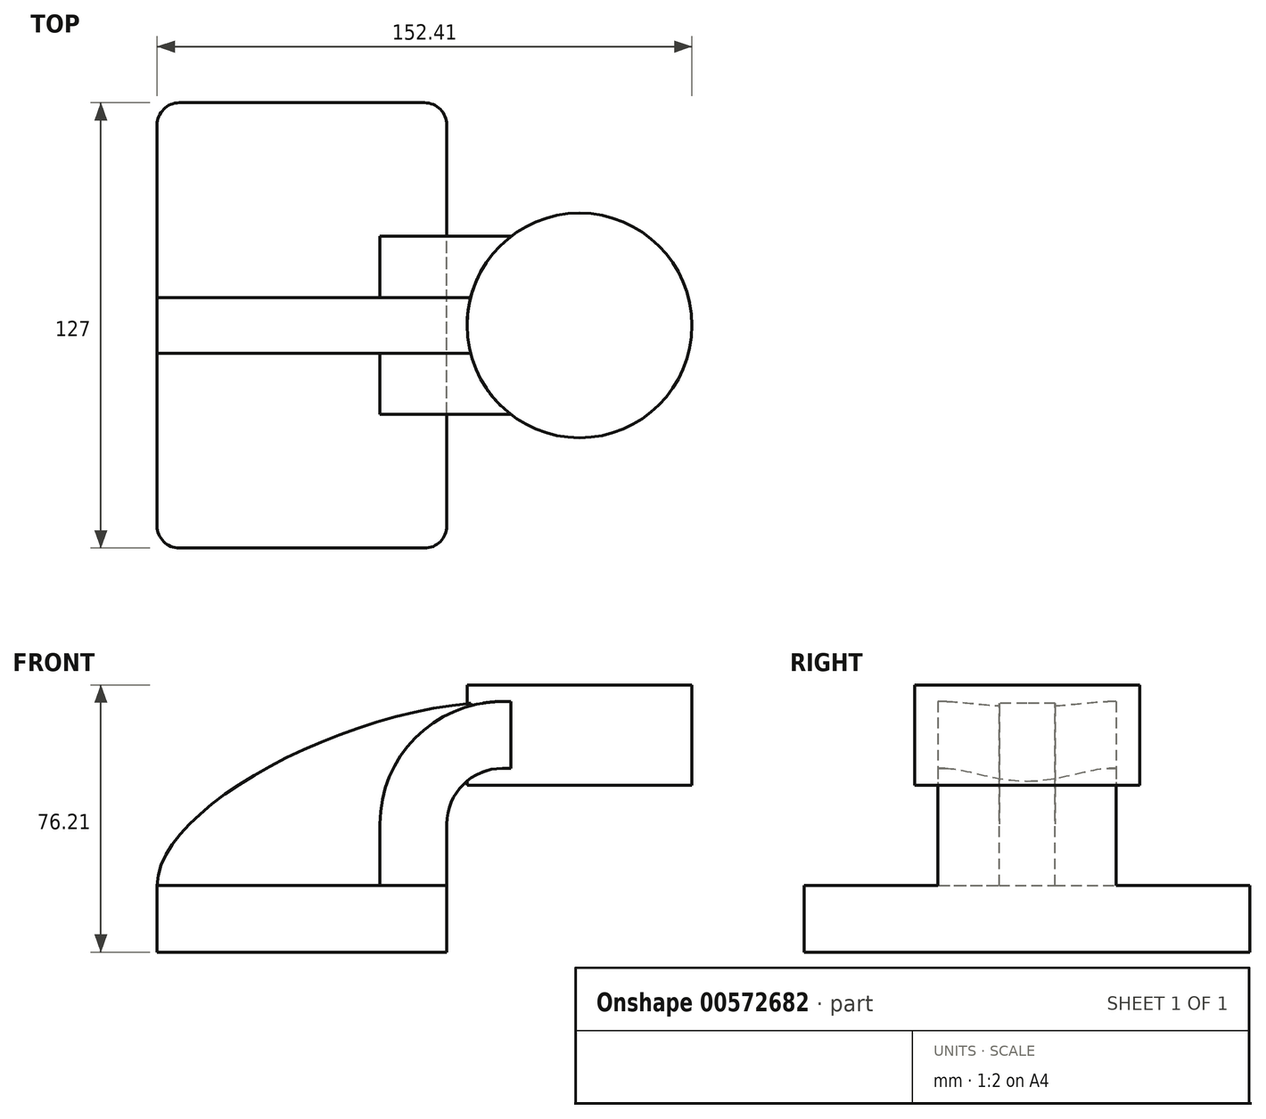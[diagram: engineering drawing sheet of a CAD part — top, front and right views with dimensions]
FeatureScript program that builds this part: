
annotation { "Feature Type Name" : "Feature", "Feature Type Description" : "" }
export const myFeature = defineFeature(function(context is Context, id is Id, definition is map)
    precondition{}
    {
        {
            var Q0;
            Q0=qCreatedBy(makeId("Front.planeOp"),FACE);
            var sketch = newSketch(context, id + "F0", { "sketchPlane" : qUnion([Q0])});
            skLineSegment(sketch, "E0.bottom", {"start": v(-41.28, -9.53) * mm, "end": v(41.28, -9.53) * mm});
            skLineSegment(sketch, "E0.top", {"start": v(-41.28, 9.53) * mm, "end": v(41.28, 9.53) * mm});
            skLineSegment(sketch, "E0.left", {"start": v(-41.28, -9.53) * mm, "end": v(-41.28, 9.53) * mm});
            skLineSegment(sketch, "E0.right", {"start": v(41.28, -9.53) * mm, "end": v(41.28, 9.53) * mm});
            skPoint(sketch, "E0.middle", {"position": v(0, 0) * mm});
            skLineSegment(sketch, "E1", {"start": v(41.28, 9.53) * mm, "end": v(41.28, 27) * mm});
            skArc(sketch, "E2", {"start": v(41.28, 27) * mm, "mid": v(45.92, 38.23) * mm, "end": v(57.15, 42.88) * mm});
            skLineSegment(sketch, "E3", {"start": v(57.15, 42.88) * mm, "end": v(78.82, 42.88) * mm});
            skLineSegment(sketch, "E4.bottom", {"start": v(60.32, 38.1) * mm, "end": v(111.12, 38.1) * mm});
            skLineSegment(sketch, "E4.top", {"start": v(60.32, 66.67) * mm, "end": v(111.12, 66.67) * mm});
            skLineSegment(sketch, "E4.left", {"start": v(60.32, 38.1) * mm, "end": v(60.32, 66.67) * mm});
            skLineSegment(sketch, "E4.right", {"start": v(111.12, 38.1) * mm, "end": v(111.12, 66.67) * mm});
            skPoint(sketch, "E4.middle", {"position": v(85.72, 52.39) * mm});
            skLineSegment(sketch, "E5.0", {"start": v(57.15, 61.93) * mm, "end": v(78.82, 61.93) * mm});
            skArc(sketch, "E5.1", {"start": v(22.23, 27) * mm, "mid": v(32.45, 51.7) * mm, "end": v(57.15, 61.93) * mm});
            skLineSegment(sketch, "E5.2", {"start": v(22.23, 9.53) * mm, "end": v(22.23, 27) * mm});
            skLineSegment(sketch, "E6", {"start": v(79.09, 38.1) * mm, "end": v(79.09, 66.67) * mm});
            skFitSpline(sketch, "E7", {"points": [v(-41.28, 9.53) * mm, v(57.15, 61.93) * mm], "startDerivative": vector(1.26, 69.94) * mm, "endDerivative": vector(123.61, 0.5) * mm});
            skSolve(sketch);
        }
        {
            var Q0;
            Q0=makeQuery(id+"F0.imprint","IMPRINT",FACE,{"disambiguationData":[TD([[makeQuery(id+"F0.imprint","IMPRINT",EDGE,{"derivedFrom":sQuery(id+"F0.wireOp",EDGE,"E0.bottom")}),1.0]])]});
            extrude(context, id + "F1", {"entities" : qUnion([Q0]), "endBound" : BoundingType.SYMMETRIC, "depth" : 127 * mm, "offsetDistance" : 25.4 * mm});
        }
        {
            var Q0;
            {var subQ5=sQuery(id+"F0.wireOp",EDGE,"E1");Q0=makeQuery(id+"F0.imprint","IMPRINT",FACE,{"disambiguationData":[TD([[makeQuery(id+"F0.imprint","IMPRINT",EDGE,{"derivedFrom":subQ5}),1.0]])]});}
            extrude(context, id + "F2", {"entities" : qUnion([Q0]), "operationType" : NewBodyOperationType.ADD, "endBound" : BoundingType.SYMMETRIC, "depth" : 50.8 * mm, "offsetDistance" : 25.4 * mm});
        }
        {
            var Q0;
            {var subQ3=sQuery(id+"F0.wireOp",EDGE,"E5.2");Q0=makeQuery(id+"F0.imprint","IMPRINT",FACE,{"disambiguationData":[TD([[makeQuery(id+"F0.imprint","IMPRINT",EDGE,{"derivedFrom":subQ3}),1.0]])]});}
            extrude(context, id + "F3", {"entities" : qUnion([Q0]), "operationType" : NewBodyOperationType.ADD, "endBound" : BoundingType.SYMMETRIC, "depth" : 15.88 * mm, "offsetDistance" : 25.4 * mm});
        }
        {
            var Q0;
            {var subQ0=sQuery(id+"F0.wireOp",EDGE,"E4.right");Q0=makeQuery(id+"F0.imprint","IMPRINT",FACE,{"disambiguationData":[TD([[makeQuery(id+"F0.imprint","IMPRINT",EDGE,{"derivedFrom":subQ0}),1.0]])]});}
            var Q1;
            Q1=sQuery(id+"F0.wireOp",EDGE,"E6");
            revolve(context, id + "F4", {"operationType" : NewBodyOperationType.ADD, "entities" : qUnion([Q0]), "axis" : qUnion([Q1]), "revolveType" : RevolveType.FULL});
        }
        {
            var Q0;
            Q0=makeQuery(id+"F1.opExtrude","CAP_EDGE",EDGE,{"disambiguationData":[OSD([sQuery(id+"F0.wireOp",EDGE,"E0.right")])],"isStart":false});
            var Q1;
            Q1=makeQuery(id+"F1.opExtrude","CAP_EDGE",EDGE,{"disambiguationData":[OSD([sQuery(id+"F0.wireOp",EDGE,"E0.left")])],"isStart":false});
            var Q2;
            Q2=makeQuery(id+"F1.opExtrude","CAP_EDGE",EDGE,{"disambiguationData":[OSD([sQuery(id+"F0.wireOp",EDGE,"E0.right")])],"isStart":true});
            var Q3;
            Q3=makeQuery(id+"F1.opExtrude","CAP_EDGE",EDGE,{"disambiguationData":[OSD([sQuery(id+"F0.wireOp",EDGE,"E0.left")])],"isStart":true});
            fillet(context, id + "F5", {"entities" : qUnion([Q0, Q1, Q2, Q3]), "radius" : 6.35 * mm, "tangentPropagation" : true, "allowEdgeOverflow" : false});
        }
    });
